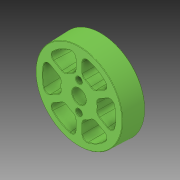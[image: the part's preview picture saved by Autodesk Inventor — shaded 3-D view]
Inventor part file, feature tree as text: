
AUTODESK INVENTOR PART (.ipt)
format: ipt  version: 2018 (Build 220112000, 112)  size: 685,568 bytes
history: native  units: in
note: dims shown in document units (in); Inventor stores cm internally (conversion verified against a paired STEP export)
features: fillet x1
ambient origin geometry x8: Origin, YZ Plane, XZ Plane, XY Plane, X Axis, Y Axis, Z Axis, Center Point
bodies: Solid1 (feature_tree)
feature tree (1):
  fillet  "Fillet3"  [1 undecoded]
note: 1 required parameter value undecoded (feature->parameter linkage not recoverable at this tier; creation-order binding heuristic only, values carry confidence <= 0.55)
